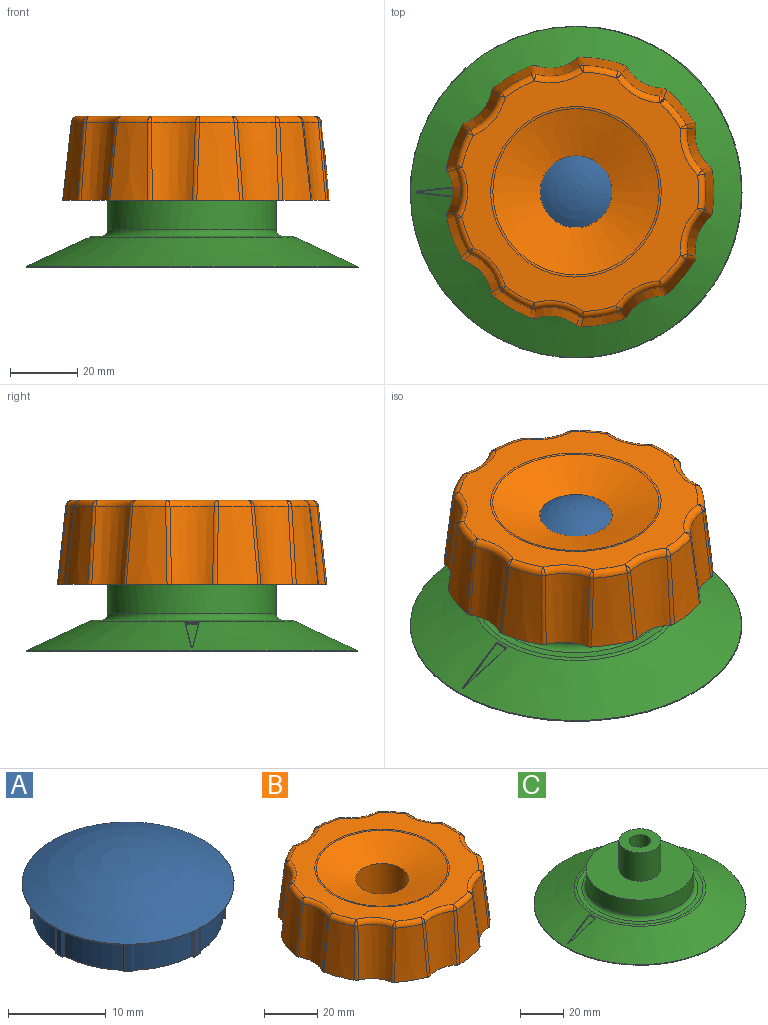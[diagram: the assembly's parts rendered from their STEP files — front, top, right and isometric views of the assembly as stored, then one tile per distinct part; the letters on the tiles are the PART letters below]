
ASSEMBLY  parts=3 mates=2
PART A: 196 faces, bbox 23.5x23.5x6.8 mm
  f0: plane 21.61x21.61mm, normal (0,0,-1), area 59.6mm2, adj f35,f37,f39,f40,f45,f49,f50,f54
  f1: plane 19.8x19.8mm, normal (0,0,-1), area 294.3mm2, adj f42,f43,f47,f52,f53,f57,f62,f66
  f2: cylinder r=9.75mm len=5.87mm, axis (0,0,-1), area 24.6mm2, adj f158,f159,f167,f168
  f3: cylinder r=9.75mm len=5.87mm, axis (0,0,-1), area 24.6mm2, adj f118,f119,f127,f128
  f4: cylinder r=9.75mm len=5.87mm, axis (0,0,-1), area 24.6mm2, adj f78,f79,f87,f88
  f5: cylinder r=9.75mm len=5.87mm, axis (0,0,-1), area 24.6mm2, adj f38,f39,f47,f48
  f6: cylinder r=9.75mm len=5.87mm, axis (0,0,-1), area 24.6mm2, adj f60,f61,f71,f72
  f7: cylinder r=9.75mm len=5.87mm, axis (0,0,-1), area 24.6mm2, adj f100,f101,f111,f112
  f8: cylinder r=9.75mm len=5.87mm, axis (0,0,-1), area 24.6mm2, adj f140,f141,f151,f152
  f9: cylinder r=9.75mm len=5.87mm, axis (0,0,-1), area 24.6mm2, adj f181,f182,f190,f191
  f10: sphere r=22.83mm, area 391.7mm2, adj f195
  f11: plane 3.8x0.07mm, normal (1,0,0), area 0.3mm2, adj f150,f151,f161,f162
  f12: plane 3.8x0.8mm, normal (0,-1,0), area 3mm2, adj f160,f161,f171,f172
  f13: plane 3.8x0.07mm, normal (-1,0,0), area 0.3mm2, adj f170,f171,f182,f183
  f14: plane 3.8x0.05mm, normal (0.71,0.71,0), area 0.3mm2, adj f110,f111,f121,f122
  f15: plane 3.8x0.57mm, normal (0.71,-0.71,0), area 3mm2, adj f120,f121,f131,f132
  f16: plane 3.8x0.05mm, normal (-0.71,-0.71,0), area 0.3mm2, adj f130,f131,f141,f142
  f17: plane 3.8x0.07mm, normal (0,1,0), area 0.3mm2, adj f70,f71,f81,f82
  f18: plane 3.8x0.8mm, normal (1,0,0), area 3mm2, adj f80,f81,f91,f92
  f19: plane 3.8x0.07mm, normal (0,-1,0), area 0.3mm2, adj f90,f91,f101,f102
  f20: plane 3.8x0.05mm, normal (-0.71,0.71,0), area 0.3mm2, adj f35,f38,f41,f42
  f21: plane 3.8x0.57mm, normal (0.71,0.71,0), area 3mm2, adj f40,f41,f51,f52
  f22: plane 3.8x0.05mm, normal (0.71,-0.71,0), area 0.3mm2, adj f50,f51,f61,f62
  f23: plane 3.8x0.07mm, normal (-1,0,0), area 0.3mm2, adj f68,f69,f77,f78
  f24: plane 3.8x0.8mm, normal (0,1,0), area 3mm2, adj f58,f59,f67,f68
  f25: plane 3.8x0.07mm, normal (1,0,0), area 0.3mm2, adj f48,f49,f57,f58
  f26: plane 3.8x0.05mm, normal (-0.71,-0.71,0), area 0.3mm2, adj f108,f109,f117,f118
  f27: plane 3.8x0.57mm, normal (-0.71,0.71,0), area 3mm2, adj f98,f99,f107,f108
  f28: plane 3.8x0.05mm, normal (0.71,0.71,0), area 0.3mm2, adj f88,f89,f97,f98
  f29: plane 3.8x0.07mm, normal (0,-1,0), area 0.3mm2, adj f148,f149,f157,f158
  f30: plane 3.8x0.8mm, normal (-1,0,0), area 3mm2, adj f138,f139,f147,f148
  f31: plane 3.8x0.07mm, normal (0,1,0), area 0.3mm2, adj f128,f129,f137,f138
  f32: plane 3.8x0.05mm, normal (0.71,-0.71,0), area 0.3mm2, adj f180,f189,f190,f194
  f33: plane 3.8x0.57mm, normal (-0.71,-0.71,0), area 3mm2, adj f178,f179,f188,f189
  f34: plane 3.8x0.05mm, normal (-0.71,0.71,0), area 0.3mm2, adj f168,f169,f177,f178
  f35: cylinder r=0.1mm len=0.12mm, axis (0.71,0.71,0), area 0mm2, adj f0,f20,f36,f37
  f36: sphere r=0.1mm, area 0mm2, adj f35,f38,f39
  f37: torus R=0.2mm, axis (0,0,1), area 0mm2, adj f0,f35,f40,f41
  f38: cylinder r=0.1mm len=3.8mm, axis (0,0,-1), area 0.6mm2, adj f5,f20,f36,f43
  f39: torus R=9.85mm, axis (0,0,1), area 1mm2, adj f0,f5,f36,f44
  f40: cylinder r=0.1mm len=0.64mm, axis (0.71,-0.71,0), area 0.1mm2, adj f0,f21,f37,f45
  f41: cylinder r=0.1mm len=3.8mm, axis (0,0,1), area 0.6mm2, adj f20,f21,f37,f46
  f42: cylinder r=0.1mm len=0.12mm, axis (-0.71,-0.71,0), area 0mm2, adj f1,f20,f43,f46
  f43: torus R=0.2mm, axis (0,0,1), area 0mm2, adj f1,f38,f42,f47
  f44: sphere r=0.1mm, area 0mm2, adj f39,f48,f49
  f45: torus R=0.2mm, axis (0,0,1), area 0mm2, adj f0,f40,f50,f51
  f46: sphere r=0.1mm, area 0mm2, adj f41,f42,f52
  f47: torus R=9.65mm, axis (0,0,1), area 1mm2, adj f1,f5,f43,f53
  f48: cylinder r=0.1mm len=3.8mm, axis (0,0,-1), area 0.6mm2, adj f5,f25,f44,f53
  f49: cylinder r=0.1mm len=0.1mm, axis (0,-1,0), area 0mm2, adj f0,f25,f44,f54
  f50: cylinder r=0.1mm len=0.12mm, axis (-0.71,-0.71,0), area 0mm2, adj f0,f22,f45,f55
  f51: cylinder r=0.1mm len=3.8mm, axis (0,0,-1), area 0.6mm2, adj f21,f22,f45,f56
  f52: cylinder r=0.1mm len=0.64mm, axis (-0.71,0.71,0), area 0.1mm2, adj f1,f21,f46,f56
  f53: torus R=0.2mm, axis (0,0,1), area 0mm2, adj f1,f47,f48,f57
  f54: torus R=0.2mm, axis (0,0,1), area 0mm2, adj f0,f49,f58,f59
  f55: sphere r=0.1mm, area 0mm2, adj f50,f60,f61
  f56: sphere r=0.1mm, area 0mm2, adj f51,f52,f62
  f57: cylinder r=0.1mm len=0.1mm, axis (0,1,0), area 0mm2, adj f1,f25,f53,f63
  f58: cylinder r=0.1mm len=3.8mm, axis (0,0,-1), area 0.6mm2, adj f24,f25,f54,f63
  f59: cylinder r=0.1mm len=0.8mm, axis (1,0,0), area 0.1mm2, adj f0,f24,f54,f64
  f60: torus R=9.85mm, axis (0,0,1), area 1mm2, adj f0,f6,f55,f65
  f61: cylinder r=0.1mm len=3.8mm, axis (0,0,-1), area 0.6mm2, adj f6,f22,f55,f66
  f62: cylinder r=0.1mm len=0.12mm, axis (0.71,0.71,0), area 0mm2, adj f1,f22,f56,f66
  f63: sphere r=0.1mm, area 0mm2, adj f57,f58,f67
  f64: torus R=0.2mm, axis (0,0,1), area 0mm2, adj f0,f59,f68,f69
  f65: sphere r=0.1mm, area 0mm2, adj f60,f70,f71
  f66: torus R=0.2mm, axis (0,0,1), area 0mm2, adj f1,f61,f62,f72
  f67: cylinder r=0.1mm len=0.8mm, axis (-1,0,0), area 0.1mm2, adj f1,f24,f63,f73
  f68: cylinder r=0.1mm len=3.8mm, axis (0,0,1), area 0.6mm2, adj f23,f24,f64,f73
  f69: cylinder r=0.1mm len=0.1mm, axis (0,1,0), area 0mm2, adj f0,f23,f64,f74
  f70: cylinder r=0.1mm len=0.1mm, axis (1,0,0), area 0mm2, adj f0,f17,f65,f75
  f71: cylinder r=0.1mm len=3.8mm, axis (0,0,-1), area 0.6mm2, adj f6,f17,f65,f76
  f72: torus R=9.65mm, axis (0,0,1), area 1mm2, adj f1,f6,f66,f76
  f73: sphere r=0.1mm, area 0mm2, adj f67,f68,f77
  f74: sphere r=0.1mm, area 0mm2, adj f69,f78,f79
  f75: torus R=0.2mm, axis (0,0,1), area 0mm2, adj f0,f70,f80,f81
  f76: torus R=0.2mm, axis (0,0,1), area 0mm2, adj f1,f71,f72,f82
  f77: cylinder r=0.1mm len=0.1mm, axis (0,-1,0), area 0mm2, adj f1,f23,f73,f83
  f78: cylinder r=0.1mm len=3.8mm, axis (0,0,-1), area 0.6mm2, adj f4,f23,f74,f83
  f79: torus R=9.85mm, axis (0,0,1), area 1mm2, adj f0,f4,f74,f84
  f80: cylinder r=0.1mm len=0.8mm, axis (0,-1,0), area 0.1mm2, adj f0,f18,f75,f85
  f81: cylinder r=0.1mm len=3.8mm, axis (0,0,1), area 0.6mm2, adj f17,f18,f75,f86
  f82: cylinder r=0.1mm len=0.1mm, axis (-1,0,0), area 0mm2, adj f1,f17,f76,f86
  f83: torus R=0.2mm, axis (0,0,1), area 0mm2, adj f1,f77,f78,f87
  f84: sphere r=0.1mm, area 0mm2, adj f79,f88,f89
  f85: torus R=0.2mm, axis (0,0,1), area 0mm2, adj f0,f80,f90,f91
  f86: sphere r=0.1mm, area 0mm2, adj f81,f82,f92
  f87: torus R=9.65mm, axis (0,0,1), area 1mm2, adj f1,f4,f83,f93
  f88: cylinder r=0.1mm len=3.8mm, axis (0,0,-1), area 0.6mm2, adj f4,f28,f84,f93
  f89: cylinder r=0.1mm len=0.12mm, axis (0.71,-0.71,0), area 0mm2, adj f0,f28,f84,f94
  f90: cylinder r=0.1mm len=0.1mm, axis (-1,0,0), area 0mm2, adj f0,f19,f85,f95
  f91: cylinder r=0.1mm len=3.8mm, axis (0,0,-1), area 0.6mm2, adj f18,f19,f85,f96
  f92: cylinder r=0.1mm len=0.8mm, axis (0,1,0), area 0.1mm2, adj f1,f18,f86,f96
  f93: torus R=0.2mm, axis (0,0,1), area 0mm2, adj f1,f87,f88,f97
  f94: torus R=0.2mm, axis (0,0,1), area 0mm2, adj f0,f89,f98,f99
  f95: sphere r=0.1mm, area 0mm2, adj f90,f100,f101
  f96: sphere r=0.1mm, area 0mm2, adj f91,f92,f102
  f97: cylinder r=0.1mm len=0.12mm, axis (-0.71,0.71,0), area 0mm2, adj f1,f28,f93,f103
  f98: cylinder r=0.1mm len=3.8mm, axis (0,0,-1), area 0.6mm2, adj f27,f28,f94,f103
  f99: cylinder r=0.1mm len=0.64mm, axis (0.71,0.71,0), area 0.1mm2, adj f0,f27,f94,f104
  f100: torus R=9.85mm, axis (0,0,1), area 1mm2, adj f0,f7,f95,f105
  f101: cylinder r=0.1mm len=3.8mm, axis (0,0,-1), area 0.6mm2, adj f7,f19,f95,f106
  f102: cylinder r=0.1mm len=0.1mm, axis (1,0,0), area 0mm2, adj f1,f19,f96,f106
  f103: sphere r=0.1mm, area 0mm2, adj f97,f98,f107
  f104: torus R=0.2mm, axis (0,0,1), area 0mm2, adj f0,f99,f108,f109
  f105: sphere r=0.1mm, area 0mm2, adj f100,f110,f111
  f106: torus R=0.2mm, axis (0,0,1), area 0mm2, adj f1,f101,f102,f112
  f107: cylinder r=0.1mm len=0.64mm, axis (-0.71,-0.71,0), area 0.1mm2, adj f1,f27,f103,f113
  f108: cylinder r=0.1mm len=3.8mm, axis (0,0,1), area 0.6mm2, adj f26,f27,f104,f113
  f109: cylinder r=0.1mm len=0.12mm, axis (-0.71,0.71,0), area 0mm2, adj f0,f26,f104,f114
  f110: cylinder r=0.1mm len=0.12mm, axis (0.71,-0.71,0), area 0mm2, adj f0,f14,f105,f115
  f111: cylinder r=0.1mm len=3.8mm, axis (0,0,-1), area 0.6mm2, adj f7,f14,f105,f116
  f112: torus R=9.65mm, axis (0,0,1), area 1mm2, adj f1,f7,f106,f116
  f113: sphere r=0.1mm, area 0mm2, adj f107,f108,f117
  f114: sphere r=0.1mm, area 0mm2, adj f109,f118,f119
  f115: torus R=0.2mm, axis (0,0,1), area 0mm2, adj f0,f110,f120,f121
  f116: torus R=0.2mm, axis (0,0,1), area 0mm2, adj f1,f111,f112,f122
  f117: cylinder r=0.1mm len=0.12mm, axis (0.71,-0.71,0), area 0mm2, adj f1,f26,f113,f123
  f118: cylinder r=0.1mm len=3.8mm, axis (0,0,-1), area 0.6mm2, adj f3,f26,f114,f123
  f119: torus R=9.85mm, axis (0,0,1), area 1mm2, adj f0,f3,f114,f124
  f120: cylinder r=0.1mm len=0.64mm, axis (-0.71,-0.71,0), area 0.1mm2, adj f0,f15,f115,f125
  f121: cylinder r=0.1mm len=3.8mm, axis (0,0,1), area 0.6mm2, adj f14,f15,f115,f126
  f122: cylinder r=0.1mm len=0.12mm, axis (-0.71,0.71,0), area 0mm2, adj f1,f14,f116,f126
  f123: torus R=0.2mm, axis (0,0,1), area 0mm2, adj f1,f117,f118,f127
  f124: sphere r=0.1mm, area 0mm2, adj f119,f128,f129
  f125: torus R=0.2mm, axis (0,0,1), area 0mm2, adj f0,f120,f130,f131
  f126: sphere r=0.1mm, area 0mm2, adj f121,f122,f132
  f127: torus R=9.65mm, axis (0,0,1), area 1mm2, adj f1,f3,f123,f133
  f128: cylinder r=0.1mm len=3.8mm, axis (0,0,-1), area 0.6mm2, adj f3,f31,f124,f133
  f129: cylinder r=0.1mm len=0.1mm, axis (1,0,0), area 0mm2, adj f0,f31,f124,f134
  f130: cylinder r=0.1mm len=0.12mm, axis (-0.71,0.71,0), area 0mm2, adj f0,f16,f125,f135
  f131: cylinder r=0.1mm len=3.8mm, axis (0,0,-1), area 0.6mm2, adj f15,f16,f125,f136
  f132: cylinder r=0.1mm len=0.64mm, axis (0.71,0.71,0), area 0.1mm2, adj f1,f15,f126,f136
  f133: torus R=0.2mm, axis (0,0,1), area 0mm2, adj f1,f127,f128,f137
  f134: torus R=0.2mm, axis (0,0,1), area 0mm2, adj f0,f129,f138,f139
  f135: sphere r=0.1mm, area 0mm2, adj f130,f140,f141
  f136: sphere r=0.1mm, area 0mm2, adj f131,f132,f142
  f137: cylinder r=0.1mm len=0.1mm, axis (-1,0,0), area 0mm2, adj f1,f31,f133,f143
  f138: cylinder r=0.1mm len=3.8mm, axis (0,0,-1), area 0.6mm2, adj f30,f31,f134,f143
  f139: cylinder r=0.1mm len=0.8mm, axis (0,1,0), area 0.1mm2, adj f0,f30,f134,f144
  f140: torus R=9.85mm, axis (0,0,1), area 1mm2, adj f0,f8,f135,f145
  f141: cylinder r=0.1mm len=3.8mm, axis (0,0,-1), area 0.6mm2, adj f8,f16,f135,f146
  f142: cylinder r=0.1mm len=0.12mm, axis (0.71,-0.71,0), area 0mm2, adj f1,f16,f136,f146
  f143: sphere r=0.1mm, area 0mm2, adj f137,f138,f147
  f144: torus R=0.2mm, axis (0,0,1), area 0mm2, adj f0,f139,f148,f149
  f145: sphere r=0.1mm, area 0mm2, adj f140,f150,f151
  f146: torus R=0.2mm, axis (0,0,1), area 0mm2, adj f1,f141,f142,f152
  f147: cylinder r=0.1mm len=0.8mm, axis (0,-1,0), area 0.1mm2, adj f1,f30,f143,f153
  f148: cylinder r=0.1mm len=3.8mm, axis (0,0,1), area 0.6mm2, adj f29,f30,f144,f153
  f149: cylinder r=0.1mm len=0.1mm, axis (-1,0,0), area 0mm2, adj f0,f29,f144,f154
  f150: cylinder r=0.1mm len=0.1mm, axis (0,-1,0), area 0mm2, adj f0,f11,f145,f155
  f151: cylinder r=0.1mm len=3.8mm, axis (0,0,-1), area 0.6mm2, adj f8,f11,f145,f156
  f152: torus R=9.65mm, axis (0,0,1), area 1mm2, adj f1,f8,f146,f156
  f153: sphere r=0.1mm, area 0mm2, adj f147,f148,f157
  f154: sphere r=0.1mm, area 0mm2, adj f149,f158,f159
  f155: torus R=0.2mm, axis (0,0,1), area 0mm2, adj f0,f150,f160,f161
  f156: torus R=0.2mm, axis (0,0,1), area 0mm2, adj f1,f151,f152,f162
  f157: cylinder r=0.1mm len=0.1mm, axis (1,0,0), area 0mm2, adj f1,f29,f153,f163
  f158: cylinder r=0.1mm len=3.8mm, axis (0,0,-1), area 0.6mm2, adj f2,f29,f154,f163
  f159: torus R=9.85mm, axis (0,0,1), area 1mm2, adj f0,f2,f154,f164
  f160: cylinder r=0.1mm len=0.8mm, axis (-1,0,0), area 0.1mm2, adj f0,f12,f155,f165
  f161: cylinder r=0.1mm len=3.8mm, axis (0,0,1), area 0.6mm2, adj f11,f12,f155,f166
  f162: cylinder r=0.1mm len=0.1mm, axis (0,1,0), area 0mm2, adj f1,f11,f156,f166
  f163: torus R=0.2mm, axis (0,0,1), area 0mm2, adj f1,f157,f158,f167
  f164: sphere r=0.1mm, area 0mm2, adj f159,f168,f169
  f165: torus R=0.2mm, axis (0,0,1), area 0mm2, adj f0,f160,f170,f171
  f166: sphere r=0.1mm, area 0mm2, adj f161,f162,f172
  f167: torus R=9.65mm, axis (0,0,1), area 1mm2, adj f1,f2,f163,f173
  f168: cylinder r=0.1mm len=3.8mm, axis (0,0,-1), area 0.6mm2, adj f2,f34,f164,f173
  f169: cylinder r=0.1mm len=0.12mm, axis (0.71,0.71,0), area 0mm2, adj f0,f34,f164,f174
  f170: cylinder r=0.1mm len=0.1mm, axis (0,1,0), area 0mm2, adj f0,f13,f165,f175
  f171: cylinder r=0.1mm len=3.8mm, axis (0,0,-1), area 0.6mm2, adj f12,f13,f165,f176
  f172: cylinder r=0.1mm len=0.8mm, axis (1,0,0), area 0.1mm2, adj f1,f12,f166,f176
  f173: torus R=0.2mm, axis (0,0,1), area 0mm2, adj f1,f167,f168,f177
  f174: torus R=0.2mm, axis (0,0,1), area 0mm2, adj f0,f169,f178,f179
  f175: sphere r=0.1mm, area 0mm2, adj f170,f181,f182
  f176: sphere r=0.1mm, area 0mm2, adj f171,f172,f183
  f177: cylinder r=0.1mm len=0.12mm, axis (-0.71,-0.71,0), area 0mm2, adj f1,f34,f173,f184
  f178: cylinder r=0.1mm len=3.8mm, axis (0,0,-1), area 0.6mm2, adj f33,f34,f174,f184
  f179: cylinder r=0.1mm len=0.64mm, axis (-0.71,0.71,0), area 0.1mm2, adj f0,f33,f174,f185
  f180: cylinder r=0.1mm len=0.12mm, axis (-0.71,-0.71,0), area 0mm2, adj f0,f32,f185,f186
  f181: torus R=9.85mm, axis (0,0,1), area 1mm2, adj f0,f9,f175,f186
  f182: cylinder r=0.1mm len=3.8mm, axis (0,0,-1), area 0.6mm2, adj f9,f13,f175,f187
  f183: cylinder r=0.1mm len=0.1mm, axis (0,-1,0), area 0mm2, adj f1,f13,f176,f187
  f184: sphere r=0.1mm, area 0mm2, adj f177,f178,f188
  f185: torus R=0.2mm, axis (0,0,1), area 0mm2, adj f0,f179,f180,f189
  f186: sphere r=0.1mm, area 0mm2, adj f180,f181,f190
  f187: torus R=0.2mm, axis (0,0,1), area 0mm2, adj f1,f182,f183,f191
  f188: cylinder r=0.1mm len=0.64mm, axis (0.71,-0.71,0), area 0.1mm2, adj f1,f33,f184,f192
  f189: cylinder r=0.1mm len=3.8mm, axis (0,0,1), area 0.6mm2, adj f32,f33,f185,f192
  f190: cylinder r=0.1mm len=3.8mm, axis (0,0,-1), area 0.6mm2, adj f9,f32,f186,f193
  f191: torus R=9.65mm, axis (0,0,1), area 1mm2, adj f1,f9,f187,f193
  f192: sphere r=0.1mm, area 0mm2, adj f188,f189,f194
  f193: torus R=0.2mm, axis (0,0,1), area 0mm2, adj f1,f190,f191,f194
  f194: cylinder r=0.1mm len=0.12mm, axis (0.71,0.71,0), area 0mm2, adj f1,f32,f192,f193
  f195: torus R=10.8mm, axis (0,0,1), area 9mm2, adj f0,f10
PART B: 77 faces, bbox 80.7x81.6x39.8 mm
  f0: cone r=40mm half-angle=6deg, axis (0,0,-1), area 272.5mm2, adj f3,f21,f24,f73
  f1: cone r=40mm half-angle=6deg, axis (0,0,-1), area 272.5mm2, adj f3,f22,f37,f70
  f2: plane 71.1x70.36mm, normal (0,0,1), area 1735.8mm2, adj f41,f42,f45,f46,f49,f50,f53,f54
  f3: plane 80.03x79.37mm, normal (0,0,-1), area 4508.1mm2, adj f0,f1,f4,f5,f6,f7,f8,f9
  f4: cone r=40mm half-angle=6deg, axis (0,0,-1), area 272.5mm2, adj f3,f23,f26,f65
  f5: cone r=40mm half-angle=6deg, axis (0,0,-1), area 272.5mm2, adj f3,f25,f28,f57
  f6: cone r=40mm half-angle=6deg, axis (0,0,-1), area 272.5mm2, adj f3,f27,f30,f49
  f7: cone r=40mm half-angle=6deg, axis (0,0,-1), area 272.5mm2, adj f3,f29,f32,f41
  f8: cone r=40mm half-angle=6deg, axis (0,0,-1), area 272.5mm2, adj f3,f31,f34,f46
  f9: cone r=40mm half-angle=6deg, axis (0,0,-1), area 272.5mm2, adj f3,f33,f36,f54
  f10: cone r=40mm half-angle=6deg, axis (0,0,-1), area 272.5mm2, adj f3,f35,f38,f62
  f11: cone r=12.5mm half-angle=6deg, axis (0,0,1), area 307.9mm2, adj f3,f37,f38,f66
  f12: cone r=12.5mm half-angle=6deg, axis (0,0,1), area 307.9mm2, adj f3,f35,f36,f58
  f13: cone r=12.5mm half-angle=6deg, axis (0,0,1), area 307.9mm2, adj f3,f33,f34,f50
  f14: cone r=12.5mm half-angle=6deg, axis (0,0,1), area 307.9mm2, adj f3,f31,f32,f42
  f15: cone r=12.5mm half-angle=6deg, axis (0,0,1), area 307.9mm2, adj f3,f29,f30,f45
  f16: cone r=12.5mm half-angle=6deg, axis (0,0,1), area 307.9mm2, adj f3,f27,f28,f53
  f17: cone r=12.5mm half-angle=6deg, axis (0,0,1), area 307.9mm2, adj f3,f25,f26,f61
  f18: cone r=12.5mm half-angle=6deg, axis (0,0,1), area 307.9mm2, adj f3,f23,f24,f69
  f19: cone r=12.5mm half-angle=6deg, axis (0,0,1), area 307.9mm2, adj f3,f21,f22,f74
  f20: cone r=10mm half-angle=71.6deg, axis (0,0,1), area 1687.9mm2, adj f39,f76
  f21: bspline ~39.73x4.51mm, area 31.5mm2, adj f0,f3,f19,f75
  f22: bspline ~37.94x4.09mm, area 31.5mm2, adj f1,f3,f19,f72
  f23: bspline ~39.73x4.57mm, area 31.5mm2, adj f3,f4,f18,f67
  f24: bspline ~37.94x4.5mm, area 31.5mm2, adj f0,f3,f18,f71
  f25: bspline ~39.73x4.63mm, area 31.5mm2, adj f3,f5,f17,f59
  f26: bspline ~37.94x4.06mm, area 31.5mm2, adj f3,f4,f17,f63
  f27: bspline ~39.73x4.46mm, area 31.5mm2, adj f3,f6,f16,f51
  f28: bspline ~37.94x4.54mm, area 31.5mm2, adj f3,f5,f16,f55
  f29: bspline ~39.73x4.74mm, area 31.5mm2, adj f3,f7,f15,f43
  f30: bspline ~37.94x4.29mm, area 31.5mm2, adj f3,f6,f15,f47
  f31: bspline ~39.73x4.21mm, area 31.5mm2, adj f3,f8,f14,f44
  f32: bspline ~37.94x4.44mm, area 31.5mm2, adj f3,f7,f14,f40
  f33: bspline ~39.73x4.7mm, area 31.5mm2, adj f3,f9,f13,f52
  f34: bspline ~37.94x4.38mm, area 31.5mm2, adj f3,f8,f13,f48
  f35: bspline ~39.73x4.25mm, area 31.5mm2, adj f3,f10,f12,f60
  f36: bspline ~37.94x4.33mm, area 31.5mm2, adj f3,f9,f12,f56
  f37: bspline ~39.73x4.66mm, area 31.5mm2, adj f1,f3,f11,f68
  f38: bspline ~37.94x4.47mm, area 31.5mm2, adj f3,f10,f11,f64
  f39: cylinder r=10mm len=20mm, axis (0,0,1), area 1256.6mm2, adj f3,f20
  f40: sphere r=2mm, area 2.4mm2, adj f32,f41,f42
  f41: torus R=35.57mm, axis (0,0,1), area 29.9mm2, adj f2,f7,f40,f43
  f42: torus R=16.93mm, axis (0,0,1), area 41.8mm2, adj f2,f14,f40,f44
  f43: sphere r=2mm, area 2.4mm2, adj f29,f41,f45
  f44: sphere r=2mm, area 2.4mm2, adj f31,f42,f46
  f45: torus R=16.93mm, axis (0,0,1), area 41.8mm2, adj f2,f15,f43,f47
  f46: torus R=35.57mm, axis (0,0,1), area 29.9mm2, adj f2,f8,f44,f48
  f47: sphere r=2mm, area 2.4mm2, adj f30,f45,f49
  f48: sphere r=2mm, area 2.4mm2, adj f34,f46,f50
  f49: torus R=35.57mm, axis (0,0,1), area 29.9mm2, adj f2,f6,f47,f51
  f50: torus R=16.93mm, axis (0,0,1), area 41.8mm2, adj f2,f13,f48,f52
  f51: sphere r=2mm, area 1.5mm2, adj f27,f49,f53
  f52: sphere r=2mm, area 2.4mm2, adj f33,f50,f54
  f53: torus R=16.93mm, axis (0,0,1), area 41.8mm2, adj f2,f16,f51,f55
  f54: torus R=35.57mm, axis (0,0,1), area 29.9mm2, adj f2,f9,f52,f56
  f55: sphere r=2mm, area 1.6mm2, adj f28,f53,f57
  f56: sphere r=2mm, area 1.2mm2, adj f36,f54,f58
  f57: torus R=35.57mm, axis (0,0,1), area 29.9mm2, adj f2,f5,f55,f59
  f58: torus R=16.93mm, axis (0,0,1), area 41.8mm2, adj f2,f12,f56,f60
  f59: sphere r=2mm, area 3.5mm2, adj f25,f57,f61
  f60: sphere r=2mm, area 2.4mm2, adj f35,f58,f62
  f61: torus R=16.93mm, axis (0,0,1), area 41.8mm2, adj f2,f17,f59,f63
  f62: torus R=35.57mm, axis (0,0,1), area 29.9mm2, adj f2,f10,f60,f64
  f63: sphere r=2mm, area 3.1mm2, adj f26,f61,f65
  f64: sphere r=2mm, area 2.4mm2, adj f38,f62,f66
  f65: torus R=35.57mm, axis (0,0,1), area 29.9mm2, adj f2,f4,f63,f67
  f66: torus R=16.93mm, axis (0,0,1), area 41.8mm2, adj f2,f11,f64,f68
  f67: sphere r=2mm, area 2.4mm2, adj f23,f65,f69
  f68: sphere r=2mm, area 2.4mm2, adj f37,f66,f70
  f69: torus R=16.93mm, axis (0,0,1), area 41.8mm2, adj f2,f18,f67,f71
  f70: torus R=35.57mm, axis (0,0,1), area 29.9mm2, adj f1,f2,f68,f72
  f71: sphere r=2mm, area 2.4mm2, adj f24,f69,f73
  f72: sphere r=2mm, area 2.4mm2, adj f22,f70,f74
  f73: torus R=35.57mm, axis (0,0,1), area 29.9mm2, adj f0,f2,f71,f75
  f74: torus R=16.93mm, axis (0,0,1), area 41.8mm2, adj f2,f19,f72,f75
  f75: sphere r=2mm, area 2.4mm2, adj f21,f73,f74
  f76: torus R=25.32mm, axis (0,0,1), area 101.1mm2, adj f2,f20
PART C: 24 faces, bbox 106.7x106.7x36.9 mm
  f0: cone r=50mm half-angle=65deg, axis (0,0,-1), area 5090.8mm2, adj f14,f15,f16,f17,f18,f19
  f1: cylinder r=25mm len=50mm, axis (0,0,1), area 1362.5mm2, adj f2,f8
  f2: plane 50x50mm, normal (0,0,1), area 1664.8mm2, adj f1,f6
  f3: plane 58.67x58.67mm, normal (0,0,1), area 413.2mm2, adj f8,f15
  f4: plane 98.2x98.2mm, normal (0,0,-1), area 7494.6mm2, adj f5,f14
  f5: cylinder r=5mm len=36mm, axis (0,0,1), area 1131mm2, adj f4,f7
  f6: cylinder r=9.75mm len=19.5mm, axis (0,0,-1), area 980.2mm2, adj f2,f7
  f7: plane 19.5x19.5mm, normal (0,0,1), area 220.1mm2, adj f5,f6
  f8: torus R=27mm, axis (0,0,1), area 507.8mm2, adj f1,f3
  f9: plane 4x0.27mm, normal (-0.91,0,-0.42), area 1.2mm2, adj f10,f12,f16,f17,f19,f23
  f10: plane 16.08x7.68mm, normal (0.09,-0.99,0.04), area 5.1mm2, adj f9,f11,f19,f21
  f11: cylinder r=0.16mm len=0.32mm, axis (-0.42,0,0.91), area 0.1mm2, adj f10,f12,f18,f20
  f12: plane 16.08x7.68mm, normal (0.09,0.99,0.04), area 5.1mm2, adj f9,f11,f16,f22
  f13: plane 15.88x7.41mm, normal (-0.42,0,0.91), area 34mm2, adj f20,f21,f22,f23
  f14: torus R=49.1mm, axis (0,0,-1), area 167.4mm2, adj f0,f4
  f15: torus R=29.33mm, axis (0,0,1), area 246.6mm2, adj f0,f3
  f16: bspline ~24.9x11.62mm, area 2.8mm2, adj f0,f9,f12,f17,f18
  f17: bspline ~10.88x0.36mm, area 0.6mm2, adj f0,f9,f16,f19
  f18: bspline ~0.52x0.28mm, area 0.1mm2, adj f0,f11,f16,f19
  f19: bspline ~26.42x12.32mm, area 2.8mm2, adj f0,f9,f10,f17,f18
  f20: torus R=0.06mm, axis (-0.42,0,0.91), area 0.1mm2, adj f11,f13,f21,f22
  f21: cylinder r=0.1mm len=16mm, axis (-0.9,-0.1,-0.42), area 2.8mm2, adj f10,f13,f20,f23
  f22: cylinder r=0.1mm len=16mm, axis (0.9,-0.1,0.42), area 2.8mm2, adj f12,f13,f20,f23
  f23: cylinder r=0.1mm len=4mm, axis (0,1,0), area 0.6mm2, adj f9,f13,f21,f22
PLACE A t=(5.77,2.43,68.22)mm
PLACE B t=(5.77,2.43,68.22)mm
PLACE C t=(5.77,2.43,68.22)mm
MATE fastened A.f2 <-> C.f6  axis (0,0,-1) through (5.77,2.43,84.22)mm
MATE fastened C.f1 <-> B.f20  axis (0,0,1) through (5.77,2.43,68.22)mm
